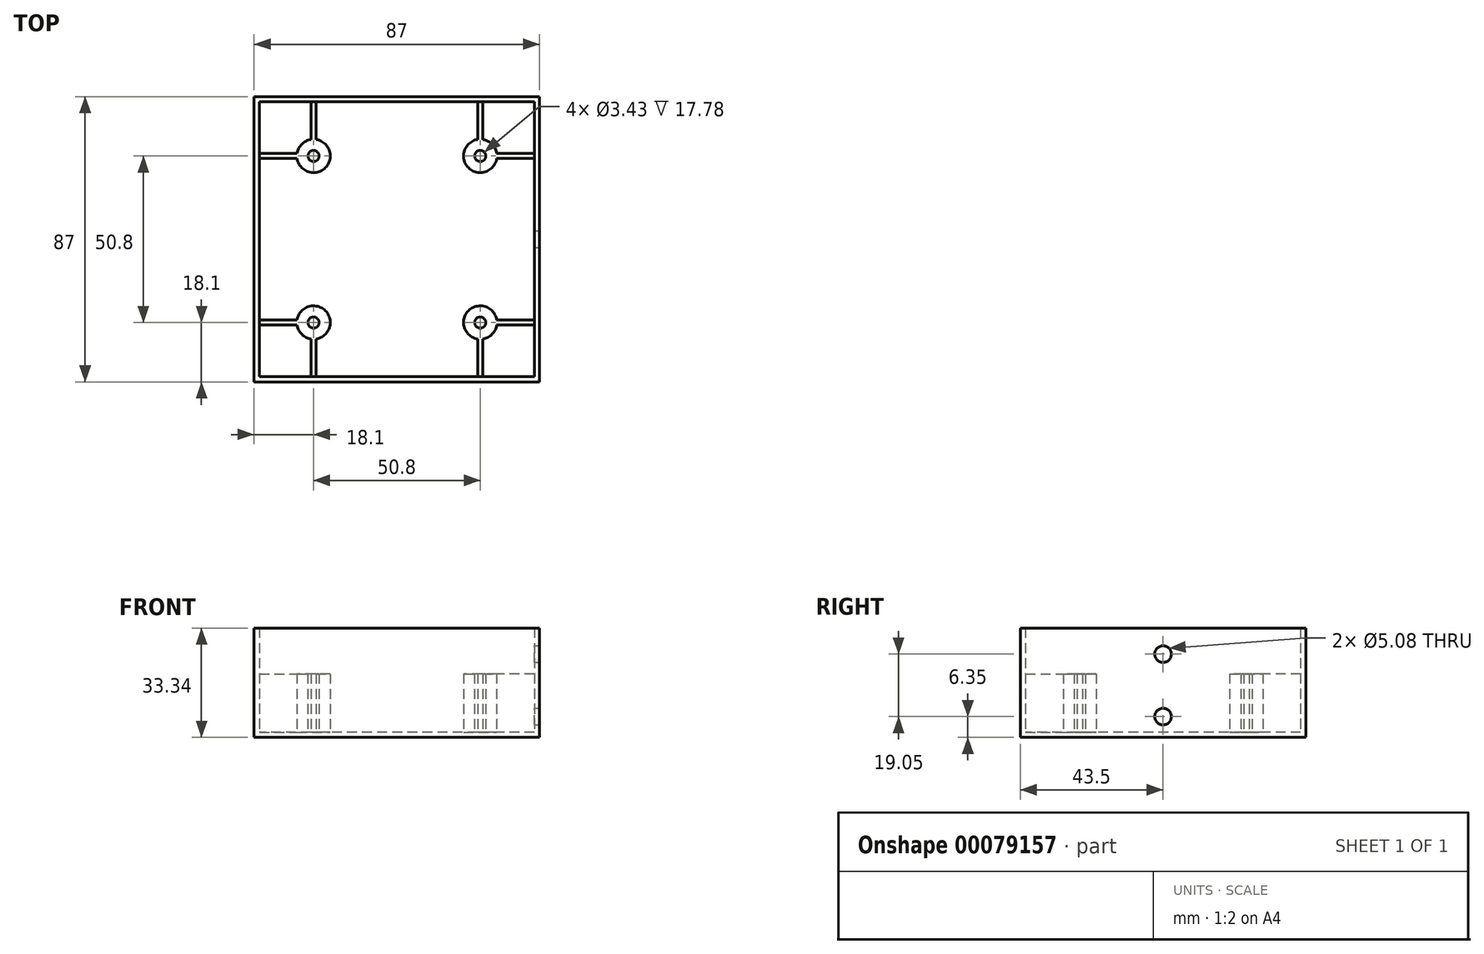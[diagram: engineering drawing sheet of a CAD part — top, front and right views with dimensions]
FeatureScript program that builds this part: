
annotation { "Feature Type Name" : "Feature", "Feature Type Description" : "" }
export const myFeature = defineFeature(function(context is Context, id is Id, definition is map)
    precondition{}
    {
        {
            var Q0;
            Q0=qCreatedBy(makeId("Top.planeOp"),FACE);
            var sketch = newSketch(context, id + "F0", { "sketchPlane" : qUnion([Q0])});
            skLineSegment(sketch, "E0.bottom", {"start": v(-43.5, 43.5) * mm, "end": v(43.5, 43.5) * mm});
            skLineSegment(sketch, "E0.top", {"start": v(-43.5, -43.5) * mm, "end": v(43.5, -43.5) * mm});
            skLineSegment(sketch, "E0.left", {"start": v(-43.5, 43.5) * mm, "end": v(-43.5, -43.5) * mm});
            skLineSegment(sketch, "E0.right", {"start": v(43.5, 43.5) * mm, "end": v(43.5, -43.5) * mm});
            skPoint(sketch, "E0.middle", {"position": v(0, 0) * mm});
            skSolve(sketch);
        }
        {
            var Q0;
            Q0 = qSketchRegion(id + "F0", true);
            extrude(context, id + "F1", {"entities" : qUnion([Q0]), "depth" : 1.59 * mm});
        }
        {
            var Q0;
            Q0=makeQuery(id+"F1.opExtrude","CAP_FACE",FACE,{"disambiguationData":[OSD([sQuery(id+"F0.wireOp",EDGE,"E0.bottom"),sQuery(id+"F0.wireOp",EDGE,"E0.top"),sQuery(id+"F0.wireOp",EDGE,"E0.left"),sQuery(id+"F0.wireOp",EDGE,"E0.right")])],"isStart":false});
            var sketch = newSketch(context, id + "F2", { "sketchPlane" : qUnion([Q0])});
            skLineSegment(sketch, "E1.bottom", {"start": v(43.5, 43.5) * mm, "end": v(-43.5, 43.5) * mm});
            skLineSegment(sketch, "E1.top", {"start": v(43.5, -43.5) * mm, "end": v(-43.5, -43.5) * mm});
            skLineSegment(sketch, "E1.left", {"start": v(43.5, 43.5) * mm, "end": v(43.5, -43.5) * mm});
            skLineSegment(sketch, "E1.right", {"start": v(-43.5, 43.5) * mm, "end": v(-43.5, -43.5) * mm});
            skPoint(sketch, "E1.middle", {"position": v(0, 0) * mm});
            skLineSegment(sketch, "E2.bottom", {"start": v(41.91, 41.91) * mm, "end": v(-41.91, 41.91) * mm});
            skLineSegment(sketch, "E2.top", {"start": v(41.91, -41.91) * mm, "end": v(-41.91, -41.91) * mm});
            skLineSegment(sketch, "E2.left", {"start": v(41.91, 41.91) * mm, "end": v(41.91, -41.91) * mm});
            skLineSegment(sketch, "E2.right", {"start": v(-41.91, 41.91) * mm, "end": v(-41.91, -41.91) * mm});
            skSolve(sketch);
        }
        {
            var Q0;
            Q0 = qSketchRegion(id + "F2", true);
            extrude(context, id + "F3", {"entities" : qUnion([Q0]), "operationType" : NewBodyOperationType.ADD, "depth" : 31.75 * mm});
        }
        {
            var Q0;
            Q0=makeQuery(id+"F1.opExtrude","CAP_FACE",FACE,{"disambiguationData":[OSD([sQuery(id+"F0.wireOp",EDGE,"E0.bottom"),sQuery(id+"F0.wireOp",EDGE,"E0.top"),sQuery(id+"F0.wireOp",EDGE,"E0.left"),sQuery(id+"F0.wireOp",EDGE,"E0.right")])],"isStart":false});
            var sketch = newSketch(context, id + "F4", { "sketchPlane" : qUnion([Q0])});
            skLineSegment(sketch, "E3.bottom", {"start": v(-25.4, 25.4) * mm, "end": v(25.4, 25.4) * mm, "construction": true});
            skLineSegment(sketch, "E3.top", {"start": v(-25.4, -25.4) * mm, "end": v(25.4, -25.4) * mm, "construction": true});
            skLineSegment(sketch, "E3.left", {"start": v(-25.4, 25.4) * mm, "end": v(-25.4, -25.4) * mm, "construction": true});
            skLineSegment(sketch, "E3.right", {"start": v(25.4, 25.4) * mm, "end": v(25.4, -25.4) * mm, "construction": true});
            skPoint(sketch, "E3.middle", {"position": v(0, 0) * mm});
            skCircle(sketch, "E4", {"center": v(-25.4, -25.4) * mm, "radius": 5.08 * mm});
            skLineSegment(sketch, "E5.bottom", {"start": v(-41.91, -26.2) * mm, "end": v(-30.42, -26.2) * mm});
            skLineSegment(sketch, "E5.top", {"start": v(-41.91, -24.6) * mm, "end": v(-30.42, -24.6) * mm});
            skLineSegment(sketch, "E5.left", {"start": v(-41.91, -26.2) * mm, "end": v(-41.91, -24.6) * mm});
            skLineSegment(sketch, "E5.right", {"start": v(-30.42, -26.2) * mm, "end": v(-30.42, -24.6) * mm});
            skLineSegment(sketch, "E6.bottom", {"start": v(-26.2, -41.91) * mm, "end": v(-24.6, -41.91) * mm});
            skLineSegment(sketch, "E6.top", {"start": v(-26.2, -30.42) * mm, "end": v(-24.6, -30.42) * mm});
            skLineSegment(sketch, "E6.left", {"start": v(-26.2, -41.91) * mm, "end": v(-26.2, -30.42) * mm});
            skLineSegment(sketch, "E6.right", {"start": v(-24.6, -41.91) * mm, "end": v(-24.6, -30.42) * mm});
            skLineSegment(sketch, "E7", {"start": v(-25.4, -25.4) * mm, "end": v(-43.5, -25.4) * mm, "construction": true});
            skLineSegment(sketch, "E8", {"start": v(-25.4, -25.4) * mm, "end": v(-25.4, -43.5) * mm, "construction": true});
            skCircle(sketch, "E9", {"center": v(-25.4, -25.4) * mm, "radius": 1.71 * mm});
            skCircle(sketch, "E10.MirrorC", {"center": v(-25.4, 25.4) * mm, "radius": 1.71 * mm});
            skCircle(sketch, "E11.MirrorC", {"center": v(-25.4, 25.4) * mm, "radius": 5.08 * mm});
            skLineSegment(sketch, "E12.MirrorCS", {"start": v(-24.6, 41.91) * mm, "end": v(-24.6, 30.42) * mm});
            skLineSegment(sketch, "E13.MirrorCS", {"start": v(-26.2, 41.91) * mm, "end": v(-26.2, 30.42) * mm});
            skLineSegment(sketch, "E14.MirrorCS", {"start": v(-41.91, 26.2) * mm, "end": v(-30.42, 26.2) * mm});
            skLineSegment(sketch, "E15.MirrorCS", {"start": v(-41.91, 24.6) * mm, "end": v(-30.42, 24.6) * mm});
            skLineSegment(sketch, "E16", {"start": v(-41.91, 24.6) * mm, "end": v(-41.91, 26.2) * mm});
            skLineSegment(sketch, "E17", {"start": v(-26.2, 41.91) * mm, "end": v(-24.6, 41.91) * mm});
            skLineSegment(sketch, "E18.MirrorCS", {"start": v(26.2, -41.91) * mm, "end": v(24.6, -41.91) * mm});
            skLineSegment(sketch, "E19.MirrorCS", {"start": v(41.91, -26.2) * mm, "end": v(41.91, -24.6) * mm});
            skLineSegment(sketch, "E20.MirrorCS", {"start": v(24.6, -41.91) * mm, "end": v(24.6, -30.42) * mm});
            skLineSegment(sketch, "E21.MirrorCS", {"start": v(26.2, -41.91) * mm, "end": v(26.2, -30.42) * mm});
            skLineSegment(sketch, "E22.MirrorCS", {"start": v(41.91, -26.2) * mm, "end": v(30.42, -26.2) * mm});
            skLineSegment(sketch, "E23.MirrorCS", {"start": v(41.91, -24.6) * mm, "end": v(30.42, -24.6) * mm});
            skCircle(sketch, "E24.MirrorC", {"center": v(25.4, -25.4) * mm, "radius": 5.08 * mm});
            skCircle(sketch, "E25.MirrorC", {"center": v(25.4, -25.4) * mm, "radius": 1.71 * mm});
            skLineSegment(sketch, "E26.MirrorCS", {"start": v(41.91, 24.6) * mm, "end": v(41.91, 26.2) * mm});
            skLineSegment(sketch, "E27.MirrorCS", {"start": v(41.91, 24.6) * mm, "end": v(30.42, 24.6) * mm});
            skLineSegment(sketch, "E28.MirrorCS", {"start": v(41.91, 26.2) * mm, "end": v(30.42, 26.2) * mm});
            skLineSegment(sketch, "E29.MirrorCS", {"start": v(26.2, 41.91) * mm, "end": v(24.6, 41.91) * mm});
            skLineSegment(sketch, "E30.MirrorCS", {"start": v(24.6, 41.91) * mm, "end": v(24.6, 30.42) * mm});
            skLineSegment(sketch, "E31.MirrorCS", {"start": v(26.2, 41.91) * mm, "end": v(26.2, 30.42) * mm});
            skCircle(sketch, "E32.MirrorC", {"center": v(25.4, 25.4) * mm, "radius": 1.71 * mm});
            skCircle(sketch, "E33.MirrorC", {"center": v(25.4, 25.4) * mm, "radius": 5.08 * mm});
            skSolve(sketch);
        }
        {
            var Q0;
            Q0 = qSketchRegion(id + "F4", true);
            extrude(context, id + "F5", {"entities" : qUnion([Q0]), "operationType" : NewBodyOperationType.ADD, "depth" : 17.78 * mm});
        }
        {
            var Q0;
            Q0=makeQuery(id+"F3.boolean.opBoolean","MERGE",FACE,{"derivedFrom":[makeQuery(id+"F1.opExtrude","SWEPT_FACE",FACE,{"disambiguationData":[OSD([sQuery(id+"F0.wireOp",EDGE,"E0.right")])]}),makeQuery(id+"F3.opExtrude","SWEPT_FACE",FACE,{"disambiguationData":[OSD([sQuery(id+"F2.wireOp",EDGE,"E1.left")])]})]});
            var sketch = newSketch(context, id + "F6", { "sketchPlane" : qUnion([Q0])});
            skCircle(sketch, "E34", {"center": v(0, 25.4) * mm, "radius": 2.54 * mm});
            skCircle(sketch, "E35", {"center": v(0, 6.35) * mm, "radius": 2.54 * mm});
            skSolve(sketch);
        }
        {
            var Q0;
            Q0 = qSketchRegion(id + "F6", true);
            extrude(context, id + "F7", {"entities" : qUnion([Q0]), "operationType" : NewBodyOperationType.REMOVE, "endBound" : BoundingType.UP_TO_NEXT, "oppositeDirection" : true, "depth" : 25.4 * mm});
        }
    });
